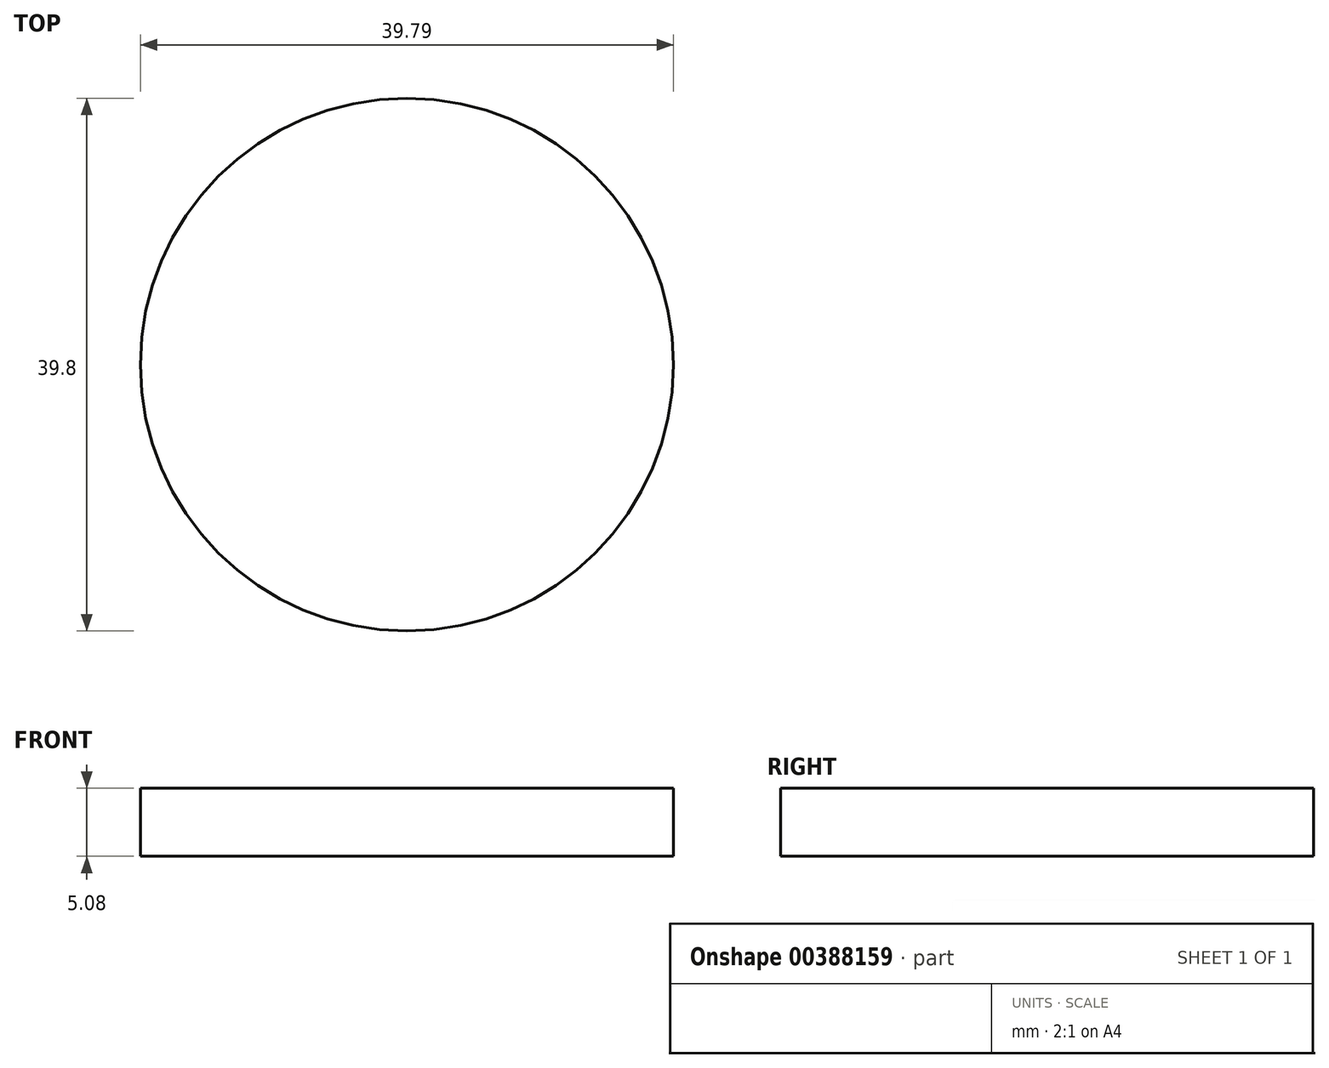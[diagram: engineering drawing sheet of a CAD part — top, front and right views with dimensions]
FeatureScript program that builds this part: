
annotation { "Feature Type Name" : "Feature", "Feature Type Description" : "" }
export const myFeature = defineFeature(function(context is Context, id is Id, definition is map)
    precondition{}
    {
        {
            var Q0;
            Q0=qCreatedBy(makeId("Top.planeOp"),FACE);
            var sketch = newSketch(context, id + "F0", { "sketchPlane" : qUnion([Q0])});
            skCircle(sketch, "E0", {"center": v(-56.9, 0) * mm, "radius": 19.9 * mm});
            skSolve(sketch);
        }
        {
            var Q0;
            Q0=makeQuery(id+"F0.imprint","IMPRINT",FACE,{"disambiguationData":[TD([[makeQuery(id+"F0.imprint","IMPRINT",EDGE,{"derivedFrom":sQuery(id+"F0.wireOp",EDGE,"E0")}),1.0]])]});
            extrude(context, id + "F1", {"entities" : qUnion([Q0]), "depth" : 5.08 * mm});
        }
    });
